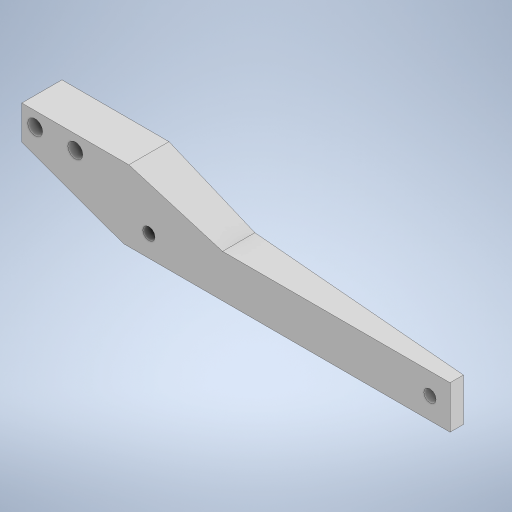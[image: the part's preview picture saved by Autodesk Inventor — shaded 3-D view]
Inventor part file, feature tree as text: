
AUTODESK INVENTOR PART (.ipt)
format: ipt  version: 2023 (Build 270158000, 158)  size: 305,152 bytes
history: native  units: mm
features: extrude x8, sketch x8, chamfer x1, projected_geometry x1
ambient origin geometry x8: Origin, YZ Plane, XZ Plane, XY Plane, X Axis, Y Axis, Z Axis, Center Point
bodies: Solid1 (feature_tree)
feature tree (18):
  extrude  "Extrusion1"  Depth=40.0mm
  extrude  "Extrusion2"  Depth=5.0mm
  extrude  "Extrusion3"  Depth=16.0mm
  extrude  "Extrusion4"  Depth=105.0mm
  extrude  "Extrusion5"  Depth=12.0mm
  extrude  "Extrusion6"  Depth=10.0mm
  chamfer  "Chamfer1"  Distance=10.0mm
  extrude  "Extrusion7"  Depth=2.0mm
  extrude  "Extrusion8"  Depth=3.0mm TaperAngle=0.0deg
  sketch  "Sketch1"  dims[d0=15.0mm d1=40.0mm]
  sketch  "Sketch2"  dims[d2=5.0mm d3=120.0mm]
  sketch  "Sketch3"  dims[d4=16.0mm d5=0.0mm d6=4.572mm]
  sketch  "Sketch4"  dims[d7=7.5mm d8=105.0mm]
  projected_geometry  "Projected Loop1"
  sketch  "Sketch5"  dims[d9=20.0mm d10=0.0mm d11=12.0mm]
  sketch  "Sketch6"  dims[d12=7.75mm d13=0.0mm d14=18.5mm d15=10.0mm d16=0.0mm]
  sketch  "Sketch7"  dims[d17=12.7mm d18=2.0mm]
  sketch  "Sketch9"  dims[d19=10.0mm d20=0.0mm d21=3.0mm d22=0.0mm d23=3.0mm d24=2.0mm d25=45.0deg d29=35.0mm d30=3.0mm d31=0.0mm d32=5.588mm d33=15.0mm d34=5.0mm d35=10.0mm d36=0.0mm]
